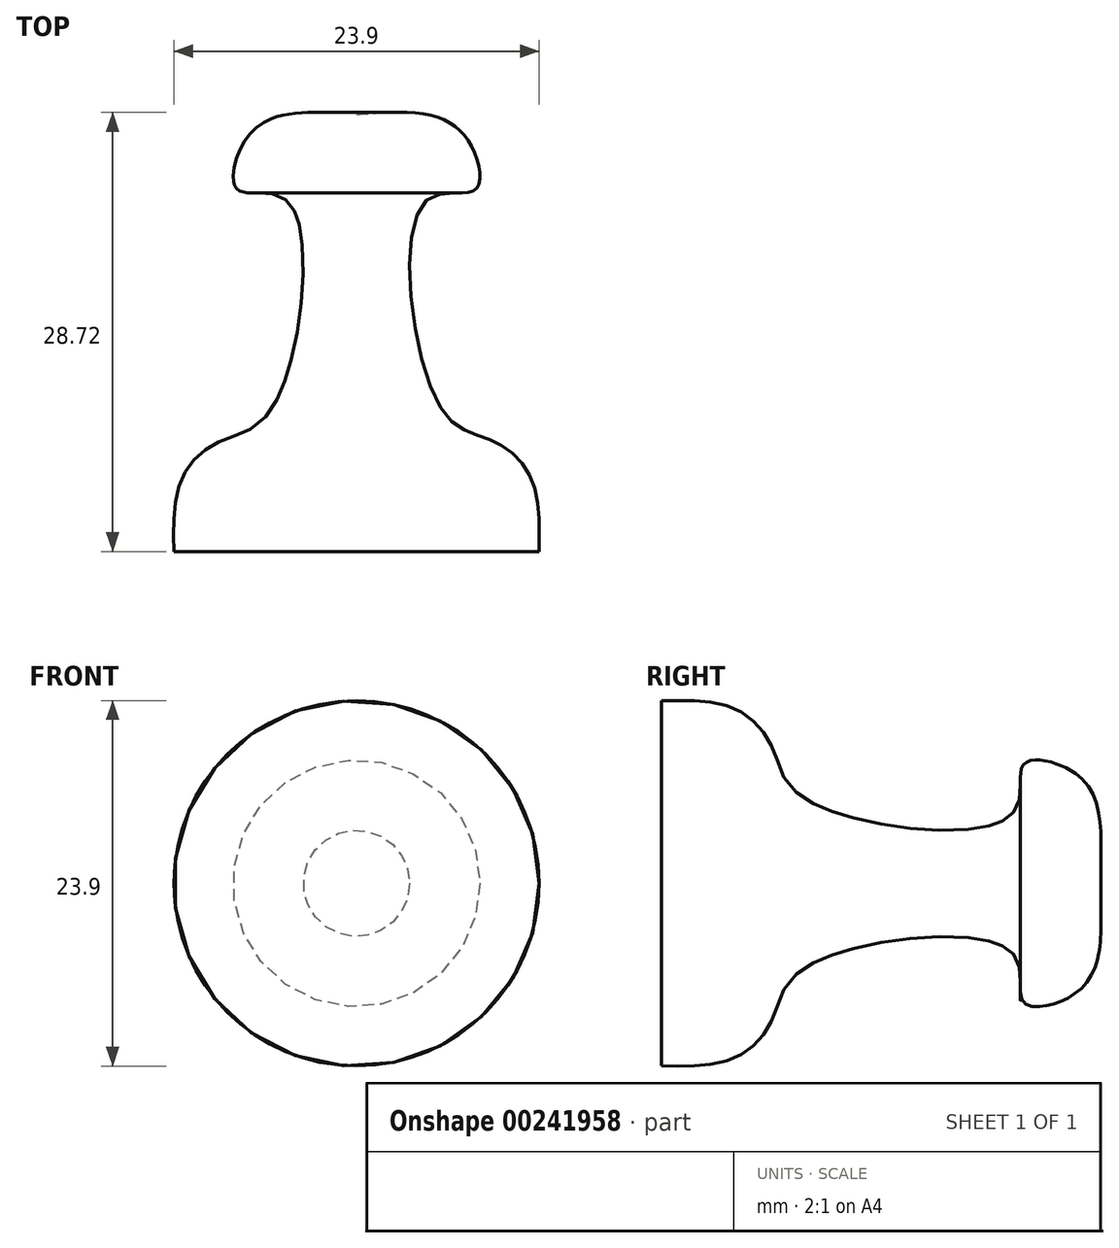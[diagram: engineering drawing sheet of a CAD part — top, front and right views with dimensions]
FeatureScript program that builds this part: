
annotation { "Feature Type Name" : "Feature", "Feature Type Description" : "" }
export const myFeature = defineFeature(function(context is Context, id is Id, definition is map)
    precondition{}
    {
        {
            var Q0;
            Q0=qCreatedBy(makeId("Top.planeOp"),FACE);
            var sketch = newSketch(context, id + "F0", { "sketchPlane" : qUnion([Q0])});
            skFitSpline(sketch, "E0", {"points": [v(0, 28.6) * mm, v(5.47, 28.35) * mm, v(7.7, 26.11) * mm, v(7.7, 23.62) * mm, v(4.48, 22.88) * mm, v(5.47, 9.45) * mm, v(8.95, 7.21) * mm, v(11.44, 4.72) * mm, v(11.94, 0) * mm], "startDerivative": vector(44.92, 3.02) * mm, "endDerivative": vector(-0.85, -40.36) * mm});
            skLineSegment(sketch, "E1", {"start": v(0, 0) * mm, "end": v(11.94, 0) * mm});
            skLineSegment(sketch, "E2", {"start": v(0, 0) * mm, "end": v(0, 28.6) * mm});
            skSolve(sketch);
        }
        {
            var Q0;
            Q0 = qSketchRegion(id + "F0", true);
            var Q1;
            Q1 = qConstructionFilter(qBodyType(qCreatedBy(id + "F0" ,EDGE), BodyType.WIRE), ConstructionObject.NO);
            var Q2;
            Q2=sQuery(id+"F0.wireOp",EDGE,"E2");
            revolve(context, id + "F1", {"entities" : qUnion([Q0]), "surfaceEntities" : qUnion([Q1]), "axis" : qUnion([Q2]), "revolveType" : RevolveType.FULL});
        }
    });
